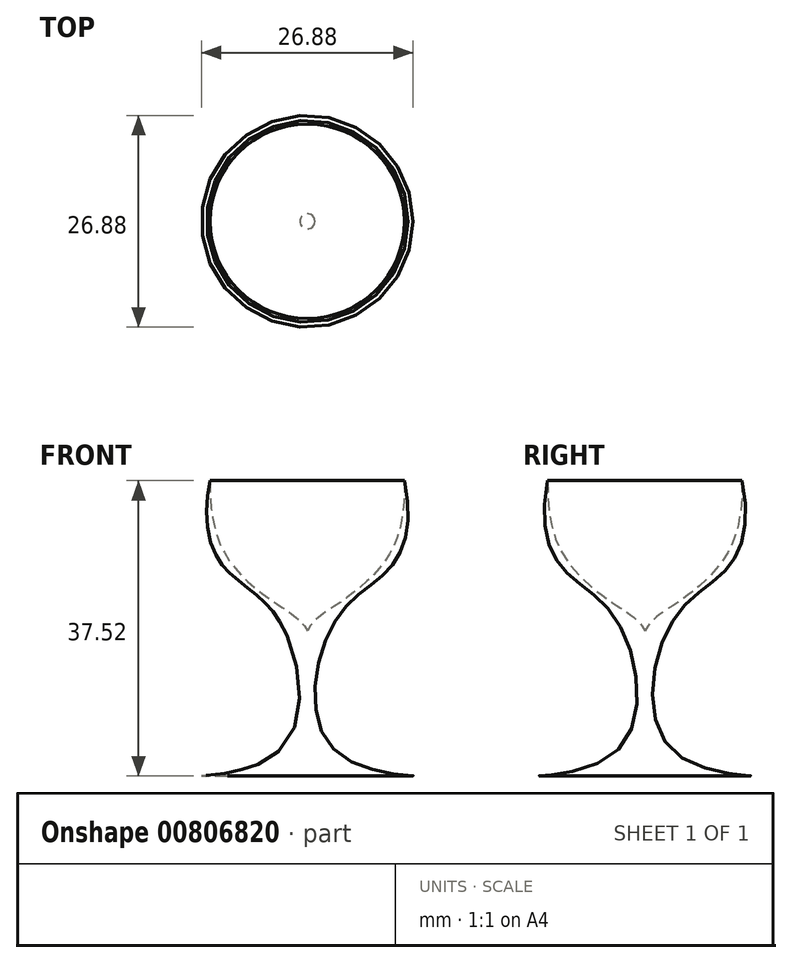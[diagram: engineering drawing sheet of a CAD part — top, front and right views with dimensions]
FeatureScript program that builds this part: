
annotation { "Feature Type Name" : "Feature", "Feature Type Description" : "" }
export const myFeature = defineFeature(function(context is Context, id is Id, definition is map)
    precondition{}
    {
        {
            var Q0;
            Q0=qCreatedBy(makeId("Front.planeOp"),FACE);
            var sketch = newSketch(context, id + "F0", { "sketchPlane" : qUnion([Q0])});
            skFitSpline(sketch, "E0", {"points": [v(12.36, 37.5) * mm, v(10.69, 26.62) * mm, v(3.61, 19.8) * mm, v(3.77, 2.98) * mm, v(13.4, 0) * mm, v(0, 0) * mm], "startDerivative": vector(15.46, -73.7) * mm, "endDerivative": vector(-31.8, 0) * mm});
            skLineSegment(sketch, "E1", {"start": v(0, 0) * mm, "end": v(0, 18.44) * mm});
            skFitSpline(sketch, "E2", {"points": [v(12.36, 37.5) * mm, v(9.9, 27.34) * mm, v(3.27, 21.44) * mm, v(0, 18.44) * mm], "startDerivative": vector(0.42, -31.77) * mm, "endDerivative": vector(-8.43, -16.47) * mm});
            skSolve(sketch);
        }
        {
            var Q0;
            Q0=makeQuery(id+"F0.imprint","IMPRINT",FACE,{"disambiguationData":[TD([[makeQuery(id+"F0.imprint","IMPRINT",EDGE,{"derivedFrom":sQuery(id+"F0.wireOp",EDGE,"E0")}),-1.0]])]});
            var Q1;
            Q1=sQuery(id+"F0.wireOp",EDGE,"E1");
            revolve(context, id + "F1", {"surfaceOperationType" : NewSurfaceOperationType.NEW, "entities" : qUnion([Q0]), "axis" : qUnion([Q1]), "revolveType" : RevolveType.FULL});
        }
    });
